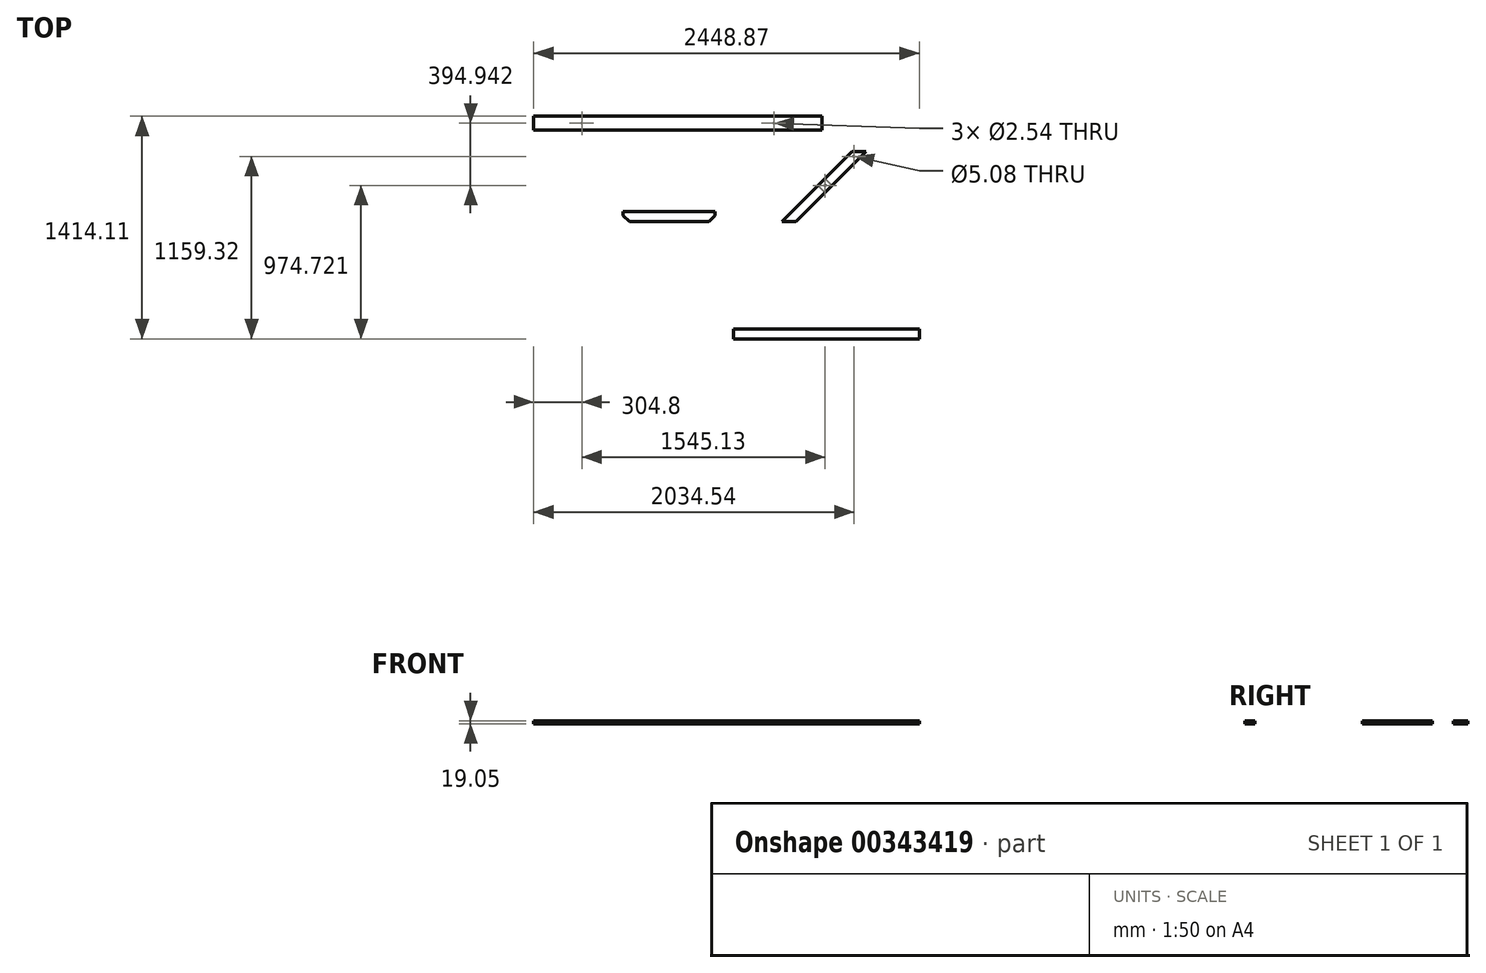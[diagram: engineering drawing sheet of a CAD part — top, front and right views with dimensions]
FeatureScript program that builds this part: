
annotation { "Feature Type Name" : "Feature", "Feature Type Description" : "" }
export const myFeature = defineFeature(function(context is Context, id is Id, definition is map)
    precondition{}
    {
        {
            var Q0;
            Q0=qCreatedBy(makeId("Top.planeOp"),FACE);
            var sketch = newSketch(context, id + "F0", { "sketchPlane" : qUnion([Q0])});
            skLineSegment(sketch, "E0", {"start": v(-1365.56, 866.44) * mm, "end": v(-1365.56, 777.54) * mm});
            skLineSegment(sketch, "E1", {"start": v(-1365.56, 777.54) * mm, "end": v(463.24, 777.54) * mm});
            skLineSegment(sketch, "E2", {"start": v(463.24, 777.54) * mm, "end": v(463.24, 866.44) * mm});
            skLineSegment(sketch, "E3", {"start": v(463.24, 866.44) * mm, "end": v(-1365.56, 866.44) * mm});
            skLineSegment(sketch, "E4", {"start": v(463.24, 822) * mm, "end": v(158.44, 822) * mm});
            skCircle(sketch, "E5", {"center": v(-1060.76, 822) * mm, "radius": 1.27 * mm});
            skCircle(sketch, "E6", {"center": v(158.44, 822) * mm, "radius": 1.27 * mm});
            skSolve(sketch);
        }
        {
            var Q0;
            Q0=qCreatedBy(makeId("Top.planeOp"),FACE);
            var sketch = newSketch(context, id + "F1", { "sketchPlane" : qUnion([Q0])});
            skLineSegment(sketch, "E7", {"start": v(-798.44, 261.02) * mm, "end": v(-798.44, 197.52) * mm});
            skLineSegment(sketch, "E8", {"start": v(-759.03, 197.52) * mm, "end": v(-253.65, 197.52) * mm});
            skLineSegment(sketch, "E9", {"start": v(-214.24, 235.62) * mm, "end": v(-214.24, 261.02) * mm});
            skLineSegment(sketch, "E10", {"start": v(-214.24, 261.02) * mm, "end": v(-798.44, 261.02) * mm});
            skLineSegment(sketch, "E11", {"start": v(-506.34, 89.83) * mm, "end": v(-506.34, 261.02) * mm});
            skPoint(sketch, "E11.endSnap0", {"position": v(-506.34, 261.02) * mm});
            skLineSegment(sketch, "E12", {"start": v(-214.24, 197.52) * mm, "end": v(-214.24, 235.62) * mm});
            skLineSegment(sketch, "E13", {"start": v(-253.65, 197.52) * mm, "end": v(-214.24, 235.62) * mm});
            skLineSegment(sketch, "E14.MirrorCS", {"start": v(-759.03, 197.52) * mm, "end": v(-798.44, 235.62) * mm});
            skSolve(sketch);
        }
        {
            var Q0;
            Q0=qCreatedBy(makeId("Top.planeOp"),FACE);
            var sketch = newSketch(context, id + "F2", { "sketchPlane" : qUnion([Q0])});
            skLineSegment(sketch, "E15", {"start": v(655.82, 643.4) * mm, "end": v(211.32, 198.9) * mm});
            skLineSegment(sketch, "E16.0", {"start": v(745.63, 643.4) * mm, "end": v(301.13, 198.9) * mm});
            skLineSegment(sketch, "E17.MirrorCS", {"start": v(484.37, 471.95) * mm, "end": v(529.28, 427.05) * mm});
            skCircle(sketch, "E18", {"center": v(484.37, 427.05) * mm, "radius": 1.27 * mm});
            skLineSegment(sketch, "E19.trimOffspring", {"start": v(483.48, 427.95) * mm, "end": v(485.27, 426.15) * mm});
            skLineSegment(sketch, "E20.trimOffspring", {"start": v(439.47, 427.05) * mm, "end": v(484.37, 382.15) * mm});
            skLineSegment(sketch, "E21.trimOffspring", {"start": v(485.27, 427.95) * mm, "end": v(483.48, 426.15) * mm});
            skPoint(sketch, "E22.trimOffspring.end.orphan", {"position": v(332.43, 275.1) * mm});
            skLineSegment(sketch, "E23", {"start": v(655.82, 643.4) * mm, "end": v(745.63, 643.4) * mm});
            skLineSegment(sketch, "E24", {"start": v(301.13, 198.9) * mm, "end": v(211.32, 198.9) * mm});
            skCircle(sketch, "E25", {"center": v(668.98, 611.65) * mm, "radius": 2.54 * mm});
            skPoint(sketch, "E26.orphan", {"position": v(624.07, 611.65) * mm});
            skPoint(sketch, "E27.orphan", {"position": v(713.88, 611.65) * mm});
            skSolve(sketch);
        }
        {
            var Q0;
            Q0=qCreatedBy(makeId("Top.planeOp"),FACE);
            var sketch = newSketch(context, id + "F3", { "sketchPlane" : qUnion([Q0])});
            skLineSegment(sketch, "E28", {"start": v(-97.8, -484.17) * mm, "end": v(-97.8, -547.67) * mm});
            skLineSegment(sketch, "E29", {"start": v(-97.8, -547.67) * mm, "end": v(1083.3, -547.67) * mm});
            skLineSegment(sketch, "E30", {"start": v(1083.3, -547.67) * mm, "end": v(1083.3, -484.17) * mm});
            skLineSegment(sketch, "E31", {"start": v(1083.3, -484.17) * mm, "end": v(-97.8, -484.17) * mm});
            skSolve(sketch);
        }
        {
            var Q0;
            Q0 = qSketchRegion(id + "F0", true);
            extrude(context, id + "F4", {"entities" : qUnion([Q0]), "depth" : 19.05 * mm});
        }
        {
            var Q0;
            {var subQ5=sQuery(id+"F1.wireOp",EDGE,"E9");Q0=makeQuery(id+"F1.imprint","IMPRINT",FACE,{"disambiguationData":[TD([[makeQuery(id+"F1.imprint","IMPRINT",EDGE,{"derivedFrom":subQ5}),1.0]])]});}
            var Q1;
            {var subQ5=sQuery(id+"F1.wireOp",EDGE,"E14.MirrorCS");Q1=makeQuery(id+"F1.imprint","IMPRINT",FACE,{"disambiguationData":[TD([[makeQuery(id+"F1.imprint","IMPRINT",EDGE,{"derivedFrom":subQ5}),-1.0]])]});}
            extrude(context, id + "F5", {"entities" : qUnion([Q0, Q1]), "depth" : 19.05 * mm});
        }
        {
            var Q0;
            Q0=makeQuery(id+"F3.imprint","IMPRINT",FACE,{"disambiguationData":[TD([[makeQuery(id+"F3.imprint","IMPRINT",EDGE,{"derivedFrom":sQuery(id+"F3.wireOp",EDGE,"E28")}),1.0]])]});
            extrude(context, id + "F6", {"entities" : qUnion([Q0]), "depth" : 19.05 * mm});
        }
        {
            var Q0;
            {var subQ2=sQuery(id+"F2.wireOp",EDGE,"E20.trimOffspring");Q0=makeQuery(id+"F2.imprint","IMPRINT",FACE,{"disambiguationData":[TD([[makeQuery(id+"F2.imprint","IMPRINT",EDGE,{"derivedFrom":subQ2}),-1.0]])]});}
            var Q1;
            {var subQ5=sQuery(id+"F2.wireOp",EDGE,"E17.MirrorCS");Q1=makeQuery(id+"F2.imprint","IMPRINT",FACE,{"disambiguationData":[TD([[makeQuery(id+"F2.imprint","IMPRINT",EDGE,{"derivedFrom":subQ5}),-1.0]])]});}
            var Q2;
            {var subQ1=sQuery(id+"F2.wireOp",EDGE,"E17.MirrorCS");Q2=makeQuery(id+"F2.imprint","IMPRINT",FACE,{"disambiguationData":[TD([[makeQuery(id+"F2.imprint","IMPRINT",EDGE,{"derivedFrom":subQ1}),1.0]])]});}
            extrude(context, id + "F7", {"entities" : qUnion([Q0, Q1, Q2]), "depth" : 19.05 * mm});
        }
        {
            var Q0;
            {var subQ5=sQuery(id+"F2.wireOp",EDGE,"E17.MirrorCS");Q0=makeQuery(id+"F2.imprint","IMPRINT",FACE,{"disambiguationData":[TD([[makeQuery(id+"F2.imprint","IMPRINT",EDGE,{"derivedFrom":subQ5}),-1.0]])]});}
            extrude(context, id + "F8", {"entities" : qUnion([Q0]), "operationType" : NewBodyOperationType.REMOVE, "oppositeDirection" : true, "depth" : -9.52 * mm});
        }
    });
